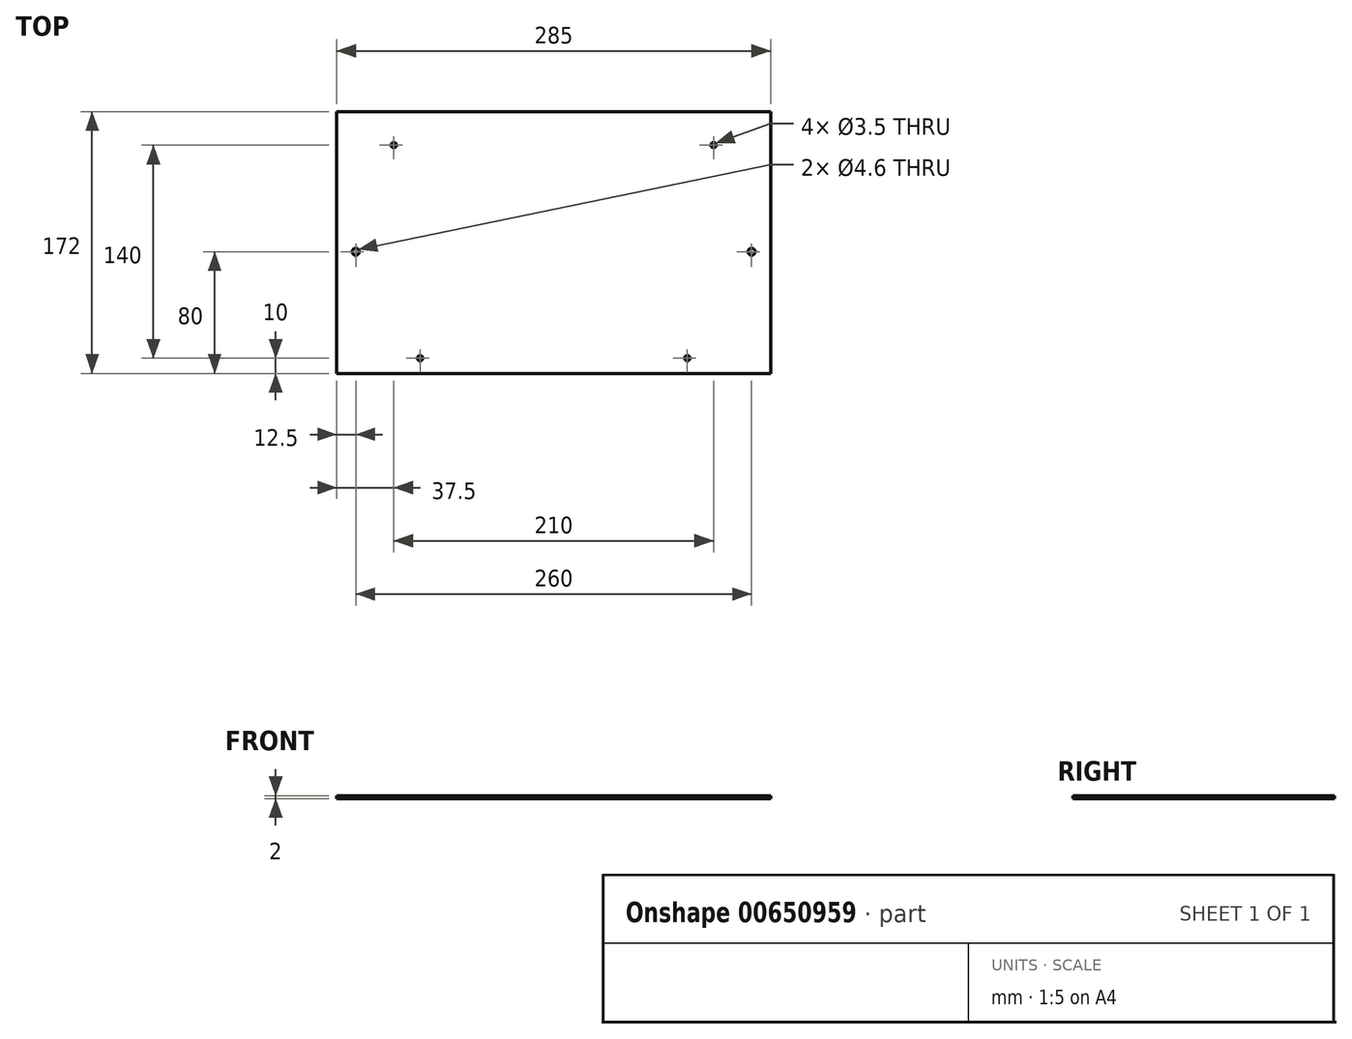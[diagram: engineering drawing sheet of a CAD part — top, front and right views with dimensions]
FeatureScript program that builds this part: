
annotation { "Feature Type Name" : "Feature", "Feature Type Description" : "" }
export const myFeature = defineFeature(function(context is Context, id is Id, definition is map)
    precondition{}
    {
        {
            var Q0;
            Q0=qCreatedBy(makeId("Top.planeOp"),FACE);
            var sketch = newSketch(context, id + "F0", { "sketchPlane" : qUnion([Q0])});
            skLineSegment(sketch, "E0.bottom", {"start": v(0, 0) * mm, "end": v(285, 0) * mm});
            skLineSegment(sketch, "E0.top", {"start": v(0, 172) * mm, "end": v(285, 172) * mm});
            skLineSegment(sketch, "E0.left", {"start": v(0, 0) * mm, "end": v(0, 172) * mm});
            skLineSegment(sketch, "E0.right", {"start": v(285, 0) * mm, "end": v(285, 172) * mm});
            skCircle(sketch, "E1", {"center": v(54.75, 10) * mm, "radius": 1.75 * mm});
            skCircle(sketch, "E2", {"center": v(230.25, 10) * mm, "radius": 1.75 * mm});
            skLineSegment(sketch, "E3", {"start": v(142.5, 0) * mm, "end": v(142.5, 172) * mm, "construction": true});
            skLineSegment(sketch, "E4", {"start": v(54.75, 10) * mm, "end": v(230.25, 10) * mm, "construction": true});
            skLineSegment(sketch, "E5", {"start": v(37.5, 150) * mm, "end": v(142.5, 150) * mm, "construction": true});
            skLineSegment(sketch, "E6", {"start": v(142.5, 150) * mm, "end": v(247.5, 150) * mm, "construction": true});
            skCircle(sketch, "E7", {"center": v(37.5, 150) * mm, "radius": 1.75 * mm});
            skCircle(sketch, "E8", {"center": v(247.5, 150) * mm, "radius": 1.75 * mm});
            skLineSegment(sketch, "E9", {"start": v(12.5, 80) * mm, "end": v(142.5, 80) * mm, "construction": true});
            skCircle(sketch, "E10", {"center": v(12.5, 80) * mm, "radius": 2.3 * mm});
            skLineSegment(sketch, "E11", {"start": v(142.5, 80) * mm, "end": v(272.5, 80) * mm, "construction": true});
            skCircle(sketch, "E12", {"center": v(272.5, 80) * mm, "radius": 2.3 * mm});
            skSolve(sketch);
        }
        {
            var Q0;
            Q0=makeQuery(id+"F0.imprint","IMPRINT",FACE,{"disambiguationData":[TD([[makeQuery(id+"F0.imprint","IMPRINT",EDGE,{"derivedFrom":sQuery(id+"F0.wireOp",EDGE,"E0.bottom")}),1.0]])]});
            extrude(context, id + "F1", {"entities" : qUnion([Q0]), "depth" : 2 * mm, "offsetDistance" : 25 * mm});
        }
    });
